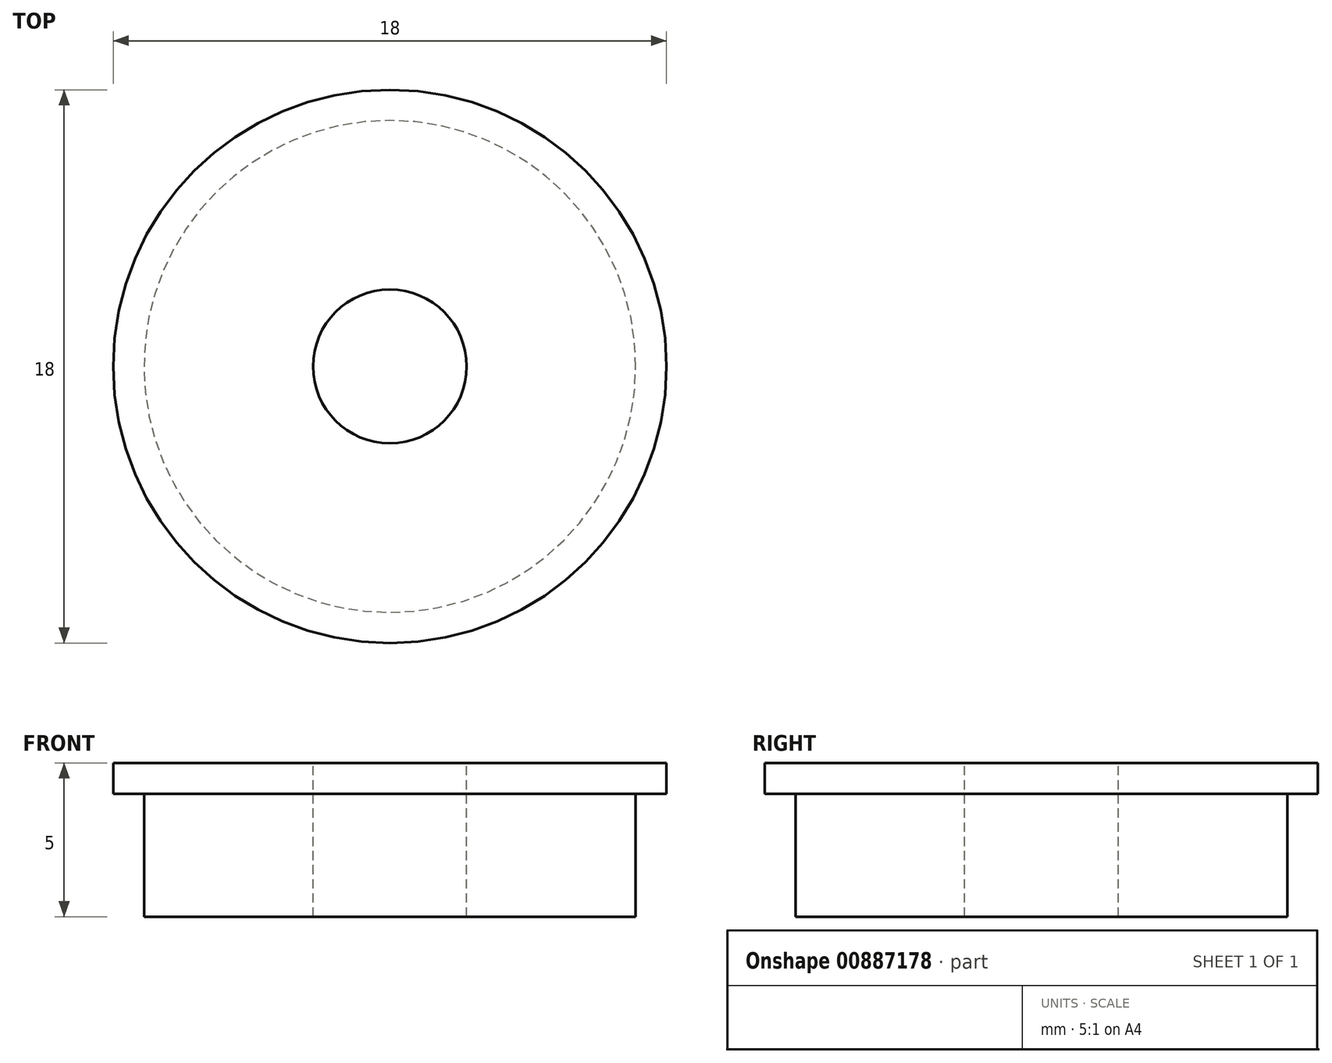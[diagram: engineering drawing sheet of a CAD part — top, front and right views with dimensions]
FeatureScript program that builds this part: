
annotation { "Feature Type Name" : "Feature", "Feature Type Description" : "" }
export const myFeature = defineFeature(function(context is Context, id is Id, definition is map)
    precondition{}
    {
        {
            var Q0;
            Q0=qCreatedBy(makeId("Right.planeOp"),FACE);
            var sketch = newSketch(context, id + "F0", { "sketchPlane" : qUnion([Q0])});
            skLineSegment(sketch, "E0.bottom", {"start": v(-8, 0) * mm, "end": v(-2.5, 0) * mm});
            skLineSegment(sketch, "E0.left", {"start": v(-8, 0) * mm, "end": v(-8, 4) * mm});
            skLineSegment(sketch, "E0.right", {"start": v(8, 0) * mm, "end": v(8, 4) * mm, "construction": true});
            skLineSegment(sketch, "E1.bottom", {"start": v(-9, 5) * mm, "end": v(-2.5, 5) * mm});
            skLineSegment(sketch, "E1.top", {"start": v(-9, 4) * mm, "end": v(-8, 4) * mm});
            skLineSegment(sketch, "E1.left", {"start": v(-9, 5) * mm, "end": v(-9, 4) * mm});
            skLineSegment(sketch, "E1.right", {"start": v(9, 5) * mm, "end": v(9, 4) * mm, "construction": true});
            skLineSegment(sketch, "E2", {"start": v(-2.5, 5) * mm, "end": v(-2.5, 0) * mm});
            skLineSegment(sketch, "E3.MirrorCS", {"start": v(2.5, 5) * mm, "end": v(2.5, 0) * mm, "construction": true});
            skLineSegment(sketch, "E4.trimOffspring", {"start": v(2.5, 5) * mm, "end": v(9, 5) * mm, "construction": true});
            skLineSegment(sketch, "E5.trimOffspring", {"start": v(8, 4) * mm, "end": v(9, 4) * mm, "construction": true});
            skLineSegment(sketch, "E6.trimOffspring", {"start": v(2.5, 0) * mm, "end": v(8, 0) * mm, "construction": true});
            skLineSegment(sketch, "E7", {"start": v(0, 6.62) * mm, "end": v(0, -4.14) * mm, "construction": true});
            skSolve(sketch);
        }
        {
            var Q0;
            Q0 = qSketchRegion(id + "F0", true);
            var Q1;
            Q1=sQuery(id+"F0.wireOp",EDGE,"E7");
            revolve(context, id + "F1", {"surfaceOperationType" : NewSurfaceOperationType.NEW, "entities" : qUnion([Q0]), "axis" : qUnion([Q1]), "revolveType" : RevolveType.FULL});
        }
    });
